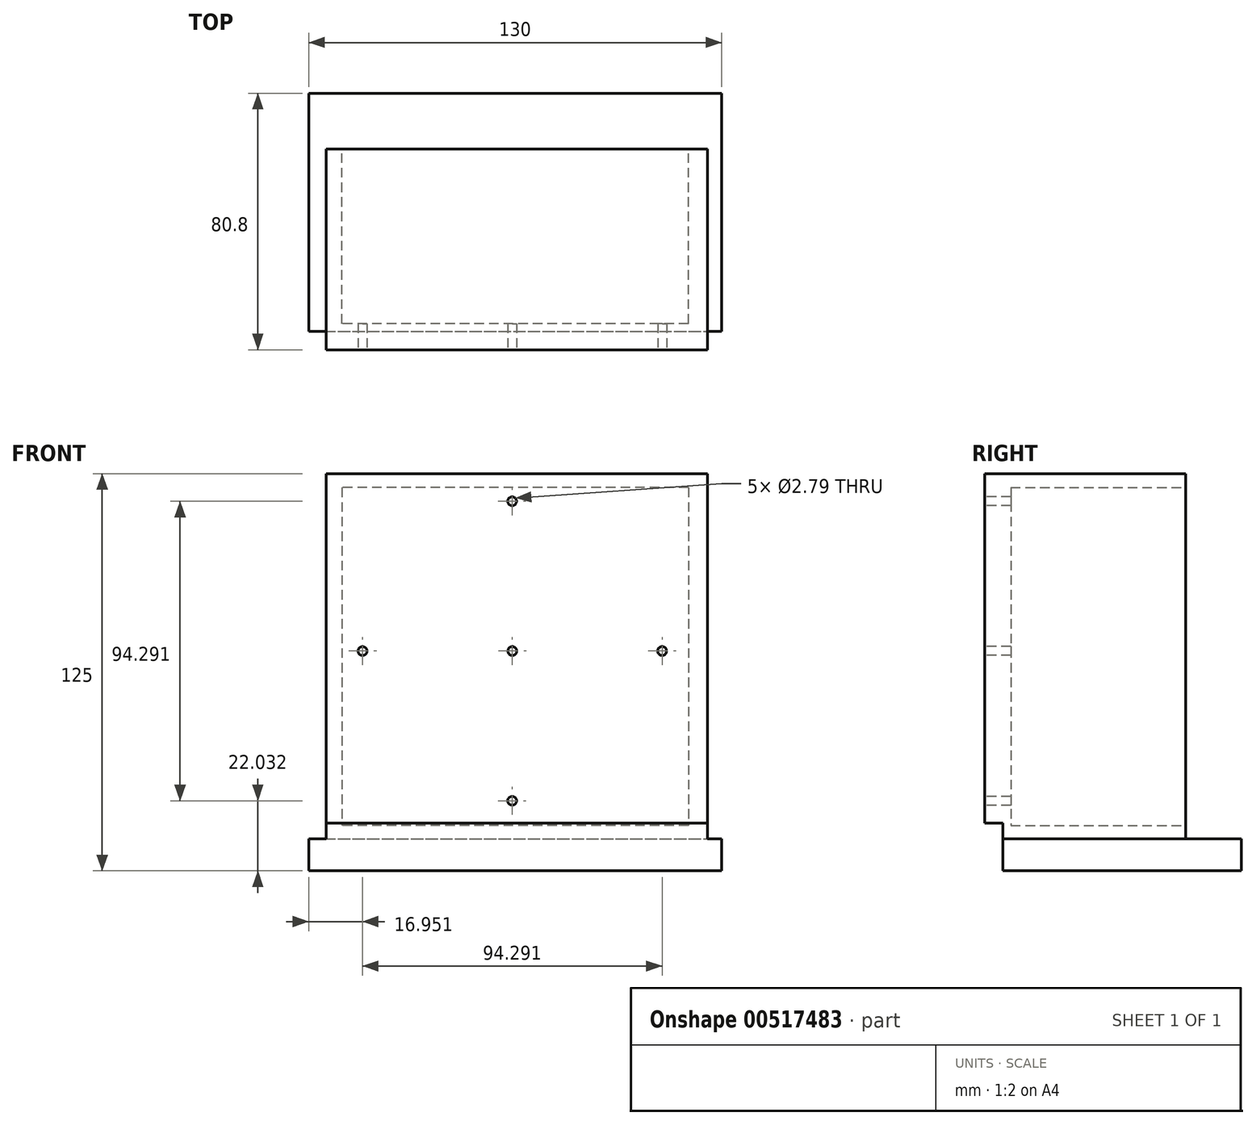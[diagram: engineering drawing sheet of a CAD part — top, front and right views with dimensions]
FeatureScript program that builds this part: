
annotation { "Feature Type Name" : "Feature", "Feature Type Description" : "" }
export const myFeature = defineFeature(function(context is Context, id is Id, definition is map)
    precondition{}
    {
        {
            var Q0;
            Q0=qCreatedBy(makeId("Top.planeOp"),FACE);
            var sketch = newSketch(context, id + "F0", { "sketchPlane" : qUnion([Q0])});
            skLineSegment(sketch, "E0.bottom", {"start": v(-64.03, 35.58) * mm, "end": v(65.97, 35.58) * mm});
            skLineSegment(sketch, "E0.top", {"start": v(-64.03, -39.42) * mm, "end": v(65.97, -39.42) * mm});
            skLineSegment(sketch, "E0.left", {"start": v(-64.03, 35.58) * mm, "end": v(-64.03, -39.42) * mm});
            skLineSegment(sketch, "E0.right", {"start": v(65.97, 35.58) * mm, "end": v(65.97, -39.42) * mm});
            skLineSegment(sketch, "E1", {"start": v(0, 0) * mm, "end": v(-98.2, 0) * mm, "construction": true});
            skLineSegment(sketch, "E2", {"start": v(0, 0) * mm, "end": v(77.32, 0) * mm, "construction": true});
            skLineSegment(sketch, "E3", {"start": v(0, 0) * mm, "end": v(0, 62.08) * mm, "construction": true});
            skLineSegment(sketch, "E4", {"start": v(0, 0) * mm, "end": v(0, -61.86) * mm, "construction": true});
            skSolve(sketch);
        }
        {
            var Q0;
            Q0=makeQuery(id+"F0.imprint","IMPRINT",FACE,{"disambiguationData":[TD([[makeQuery(id+"F0.imprint","IMPRINT",EDGE,{"derivedFrom":sQuery(id+"F0.wireOp",EDGE,"E0.bottom")}),-1.0]])]});
            extrude(context, id + "F1", {"entities" : qUnion([Q0]), "depth" : 10 * mm, "offsetDistance" : 25 * mm});
        }
        {
            var Q0;
            Q0=makeQuery(id+"F1.opExtrude","CAP_FACE",FACE,{"disambiguationData":[OSD([sQuery(id+"F0.wireOp",EDGE,"E0.bottom"),sQuery(id+"F0.wireOp",EDGE,"E0.top"),sQuery(id+"F0.wireOp",EDGE,"E0.left"),sQuery(id+"F0.wireOp",EDGE,"E0.right")])],"isStart":false});
            var sketch = newSketch(context, id + "F2", { "sketchPlane" : qUnion([Q0])});
            skLineSegment(sketch, "E5.bottom", {"start": v(-58.55, 18.06) * mm, "end": v(61.45, 18.06) * mm});
            skLineSegment(sketch, "E5.top", {"start": v(-58.55, -39.42) * mm, "end": v(61.45, -39.42) * mm});
            skLineSegment(sketch, "E5.left", {"start": v(-58.55, 18.06) * mm, "end": v(-58.55, -39.42) * mm});
            skLineSegment(sketch, "E5.right", {"start": v(61.45, 18.06) * mm, "end": v(61.45, -39.42) * mm});
            skSolve(sketch);
        }
        {
            var Q0;
            Q0=makeQuery(id+"F2.imprint","IMPRINT",FACE,{"disambiguationData":[TD([[makeQuery(id+"F2.imprint","IMPRINT",EDGE,{"derivedFrom":sQuery(id+"F2.wireOp",EDGE,"E5.bottom")}),-1.0]])]});
            extrude(context, id + "F3", {"entities" : qUnion([Q0]), "operationType" : NewBodyOperationType.ADD, "depth" : 5 * mm, "offsetDistance" : 25 * mm});
        }
        {
            var Q0;
            Q0=makeQuery(id+"F3.opExtrude","SWEPT_FACE",FACE,{"disambiguationData":[OSD([sQuery(id+"F2.wireOp",EDGE,"E5.left")])]});
            var sketch = newSketch(context, id + "F4", { "sketchPlane" : qUnion([Q0])});
            skLineSegment(sketch, "E6.bottom", {"start": v(-18.06, 15) * mm, "end": v(45.22, 15) * mm});
            skLineSegment(sketch, "E6.top", {"start": v(-18.06, 125) * mm, "end": v(45.22, 125) * mm});
            skLineSegment(sketch, "E6.left", {"start": v(-18.06, 15) * mm, "end": v(-18.06, 125) * mm});
            skLineSegment(sketch, "E6.right", {"start": v(45.22, 15) * mm, "end": v(45.22, 125) * mm});
            skSolve(sketch);
        }
        {
            var Q0;
            Q0=makeQuery(id+"F4.imprint","IMPRINT",FACE,{"disambiguationData":[TD([[makeQuery(id+"F4.imprint","IMPRINT",EDGE,{"derivedFrom":sQuery(id+"F4.wireOp",EDGE,"E6.top")}),-1.0]])]});
            extrude(context, id + "F5", {"entities" : qUnion([Q0]), "operationType" : NewBodyOperationType.ADD, "oppositeDirection" : true, "depth" : 120 * mm, "offsetDistance" : 25 * mm});
        }
        {
            var Q0;
            Q0=makeQuery(id+"F5.opExtrude","SWEPT_FACE",FACE,{"disambiguationData":[OSD([sQuery(id+"F4.wireOp",EDGE,"E6.right")])]});
            var sketch = newSketch(context, id + "F6", { "sketchPlane" : qUnion([Q0])});
            skCircle(sketch, "E7", {"center": v(0.07, 69.18) * mm, "radius": 47.15 * mm});
            skPoint(sketch, "E7.first.point", {"position": v(0, 116.32) * mm});
            skPoint(sketch, "E7.second.point", {"position": v(39.48, 43.3) * mm});
            skPoint(sketch, "E7.third.point", {"position": v(-24.27, 28.8) * mm});
            skPoint(sketch, "E8", {"position": v(0, 22.03) * mm});
            skPoint(sketch, "E9", {"position": v(47.21, 69.18) * mm});
            skPoint(sketch, "E10", {"position": v(-47.08, 69.18) * mm});
            skSolve(sketch);
        }
        {
            var Q0;
            Q0=sQuery(id+"F6.wireOp",VERTEX,"E7.first.point");
            var Q1;
            Q1=sQuery(id+"F6.wireOp",VERTEX,"E10");
            var Q2;
            Q2=sQuery(id+"F6.wireOp",VERTEX,"E8");
            var Q3;
            Q3=sQuery(id+"F6.wireOp",VERTEX,"E9");
            var Q4;
            Q4=sQuery(id+"F6.wireOp",VERTEX,"E7.center");
            var Q5;
            Q5=makeQuery(id+"F1.opExtrude","SWEPT_BODY",BODY,{"disambiguationData":[OSD([sQuery(id+"F0.wireOp",EDGE,"E0.bottom"),sQuery(id+"F0.wireOp",EDGE,"E0.top"),sQuery(id+"F0.wireOp",EDGE,"E0.left"),sQuery(id+"F0.wireOp",EDGE,"E0.right")])]});
            hole(context, id + "F7", {"style" : HoleStyle.SIMPLE, "endStyle" : HoleEndStyle.THROUGH, "standardTappedOrClearance" : lookupTablePath({ "standard" : "ANSI", "fit" : "Normal (ASME)", "size" : "#3", "type" : "Clearance" }), "standardBlindInLast" : lookupTablePath({ "fit" : "Free", "standard" : "ANSI", "size" : "#3", "type" : "Clearance" }), "holeDiameter" : 2.8 * mm, "isTappedThrough" : true, "tappedDepth" : 12.7 * mm, "tapClearance" : 3, "locations" : qUnion([Q0, Q1, Q2, Q3, Q4]), "scope" : qUnion([Q5])});
        }
        {
            var Q0;
            Q0=makeQuery(id+"F5.boolean.opBoolean","MERGE",FACE,{"derivedFrom":[makeQuery(id+"F3.opExtrude","SWEPT_FACE",FACE,{"disambiguationData":[OSD([sQuery(id+"F2.wireOp",EDGE,"E5.bottom")])]}),makeQuery(id+"F5.opExtrude","SWEPT_FACE",FACE,{"disambiguationData":[OSD([sQuery(id+"F4.wireOp",EDGE,"E6.left")])]})]});
            var sketch = newSketch(context, id + "F8", { "sketchPlane" : qUnion([Q0])});
            skLineSegment(sketch, "E11.bottom", {"start": v(-55.53, 120.61) * mm, "end": v(53.58, 120.61) * mm});
            skLineSegment(sketch, "E11.top", {"start": v(-55.53, 14.25) * mm, "end": v(53.58, 14.25) * mm});
            skLineSegment(sketch, "E11.left", {"start": v(-55.53, 120.61) * mm, "end": v(-55.53, 14.25) * mm});
            skLineSegment(sketch, "E11.right", {"start": v(53.58, 120.61) * mm, "end": v(53.58, 14.25) * mm});
            skSolve(sketch);
        }
        {
            var Q0;
            Q0=makeQuery(id+"F8.imprint","IMPRINT",FACE,{"disambiguationData":[TD([[makeQuery(id+"F8.imprint","IMPRINT",EDGE,{"derivedFrom":sQuery(id+"F8.wireOp",EDGE,"E11.bottom")}),-1.0]])]});
            extrude(context, id + "F9", {"entities" : qUnion([Q0]), "operationType" : NewBodyOperationType.REMOVE, "oppositeDirection" : true, "depth" : 55 * mm, "offsetDistance" : 25 * mm});
        }
    });
